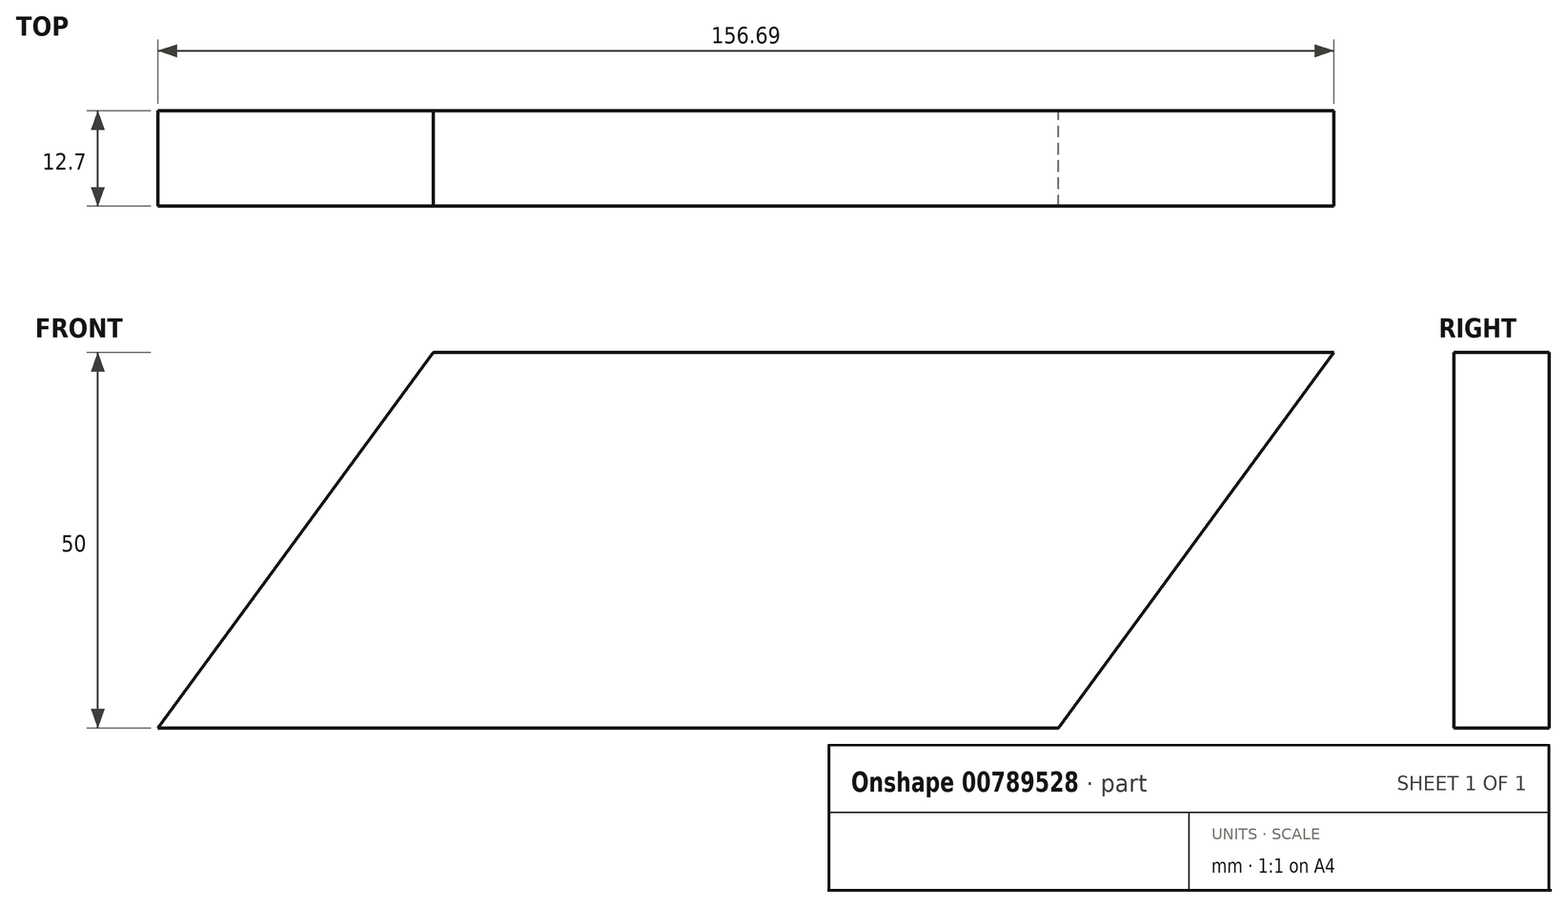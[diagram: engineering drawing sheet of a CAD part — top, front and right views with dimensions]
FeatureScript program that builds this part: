
annotation { "Feature Type Name" : "Feature", "Feature Type Description" : "" }
export const myFeature = defineFeature(function(context is Context, id is Id, definition is map)
    precondition{}
    {
        {
            var Q0;
            Q0=qCreatedBy(makeId("Front.planeOp"),FACE);
            var sketch = newSketch(context, id + "F0", { "sketchPlane" : qUnion([Q0])});
            skLineSegment(sketch, "E0", {"start": v(-55.2, 37.08) * mm, "end": v(64.8, 37.08) * mm});
            skLineSegment(sketch, "E1", {"start": v(64.8, 37.08) * mm, "end": v(28.12, -12.92) * mm});
            skLineSegment(sketch, "E2", {"start": v(28.12, -12.92) * mm, "end": v(-91.88, -12.92) * mm});
            skLineSegment(sketch, "E3", {"start": v(-91.88, -12.92) * mm, "end": v(-55.2, 37.08) * mm});
            skSolve(sketch);
        }
        {
            var Q0;
            Q0=makeQuery(id+"F0.imprint","IMPRINT",FACE,{"disambiguationData":[TD([[makeQuery(id+"F0.imprint","IMPRINT",EDGE,{"derivedFrom":sQuery(id+"F0.wireOp",EDGE,"E0")}),-1.0]])]});
            extrude(context, id + "F1", {"entities" : qUnion([Q0]), "depth" : 12.7 * mm, "offsetDistance" : 25.4 * mm});
        }
    });
